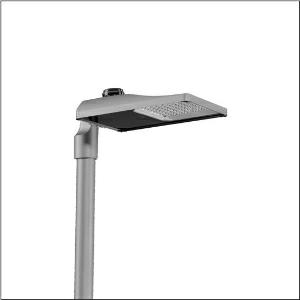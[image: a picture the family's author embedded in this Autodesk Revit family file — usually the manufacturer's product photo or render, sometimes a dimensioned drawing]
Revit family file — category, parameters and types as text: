
# Revit family: streetlight_sl_31_midi___st0_5a_5xh7b75n08na_00dd
name_source: partatom
category: Lighting Fixtures
units: mm (PartAtom-declared; Revit-internal decimal feet)

## family parameters
Cut with Voids When Loaded = No
Host = Face
Light Source = No
Part Type = Normal
Room Calculation Point = No
Round Connector Dimension = Use Diameter
Shared = No

## types (1)
- --- (1 x LED, 18640 lm, 149.4 W, 2200K)
    Apparent Load = 149 VA
    CIE Flux Codes = 43 76 97 100 100
    Color Rendering = 70
    Color Temperature = 2200K
    Default Elevation = 1800 mm
    Description = Streetlight SL 31 midi, mast luminaire, primary light control with lens, of PMMA, primary optical cover: cover, of toughened safety glass, transparent, light distribution: ST0.5a, light emission: direct distribution, primary light characteristic: asymmetric, installation type: post-top, side-entry, LED, High Power LED, rated luminous flux: 18.640lm, luminous efficacy: 125lm/W, light colour: 722, colour temperature: 2200K, control: presetting dimming linear, flexible luminous flux parameterisation, time-dependent luminous flux control, constant luminous flux control, intelligent temperature release in ECG and LED module, overheat protection, with cable H07RN-F 3x 1.5mm², mains connection: 220..240V, AC, 50/60Hz, connection cable pre-assembled, cable length: 12,5m, start of lifetime: 149W, end of service life: 163W, reduction: 66W, luminaire housing, of diecast aluminium, powder-coated, Siteco® metallic grey (DB 702S), corrosivity category C5 high according to DIN EN ISO 12944, no sealing on luminaire upper side, inclination: -15°..+20° (post-top) | -20°..+20° (side-entry), adjustable in 5° steps, mast flange (76/60mm) included as standard, multi-level sealing system, sealing non-destructively replaceable, protection rating (complete): IP66, insulation class (complete): insulation class I (protective earthing), certification: CE, ENEC, ENEC+, VDE, UKCA, impact resistance: IK09, permissible operating ambient temperature for outdoor applications: -40..+50°C, standard-compliant lighting for roads and squares, packaging unit: 1 piece

Light Distribution: ST0.5a
    Height = 79 mm
    Lamp = 1 x LED
    Lamp Light Flux = 18640 lm
    Lamp Power = 149.4 W
    Lamp count = 1
    Length = 577 mm
    Luminous efficacy = 125 lm/W
    Manufacturer = Siteco
    ModVariant = No
    Model = 5XH7B75N08NA
    Number of Poles = 1
    OnlyDefault = Yes
    Power Factor = 1
    Product Name = Streetlight SL 31 midi | ST0.5a
    Product group = mast luminaire | pylon top
    ProductGroupID = 6100
    Protection Class = Protection class I
    Protection Degree = IP 66
    RLX_Detail_Level = 1
    RLX_Emergency_Light_Flux = 0 lm
    RLX_Emergency_Type = 0
    RLX_Emergency_Type_DB = No
    RlxData = <blob elided: 54597 chars, md5=db432377>
    Socket = socket
    Standby Power = 0 W
    System Light Flux = 18641 lm
    System Power = 149 W
    Type Comments = factory setting: luminous flux: 100 % | dim-lin: 254 | 796 mA
    Type Image = l_1300282.jpg
    URL = http://relux.com
    VarID = @adj_015777
    Voltage = 0 V
    Weight = 0.00 kg
    Width = 362 mm

## geometry (parser evidence)
native form markers: Blend x4, Sweep x9
no freeform markers — native parametric forms only
